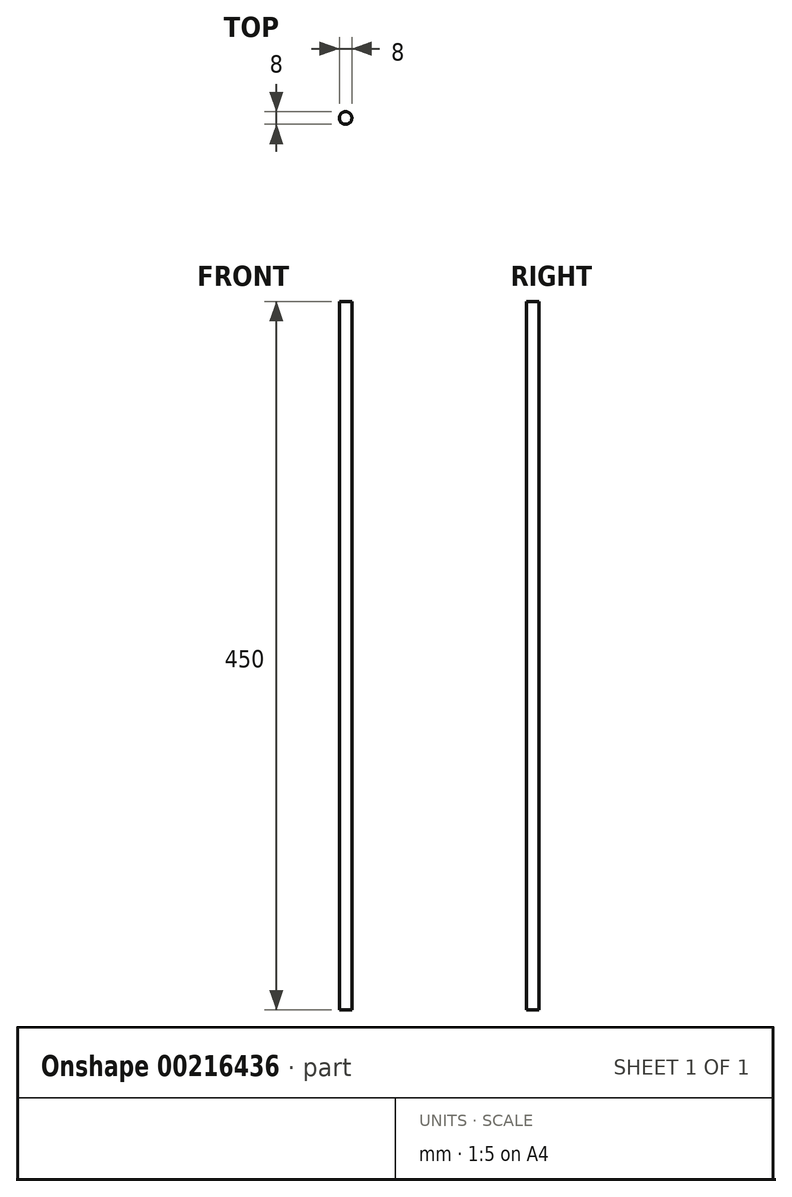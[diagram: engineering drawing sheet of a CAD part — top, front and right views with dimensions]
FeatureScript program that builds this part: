
annotation { "Feature Type Name" : "Feature", "Feature Type Description" : "" }
export const myFeature = defineFeature(function(context is Context, id is Id, definition is map)
    precondition{}
    {
        {
            var Q0;
            Q0=qCreatedBy(makeId("Top.planeOp"),FACE);
            var sketch = newSketch(context, id + "F0", { "sketchPlane" : qUnion([Q0])});
            skCircle(sketch, "E0", {"center": v(0, 0) * mm, "radius": 4 * mm});
            skSolve(sketch);
        }
        {
            var Q0;
            Q0=qSketchRegion(id+"F0",true);
            extrude(context, id + "F1", {"entities" : qUnion([Q0]), "endBound" : BoundingType.SYMMETRIC, "depth" : 450 * mm});
        }
    });
